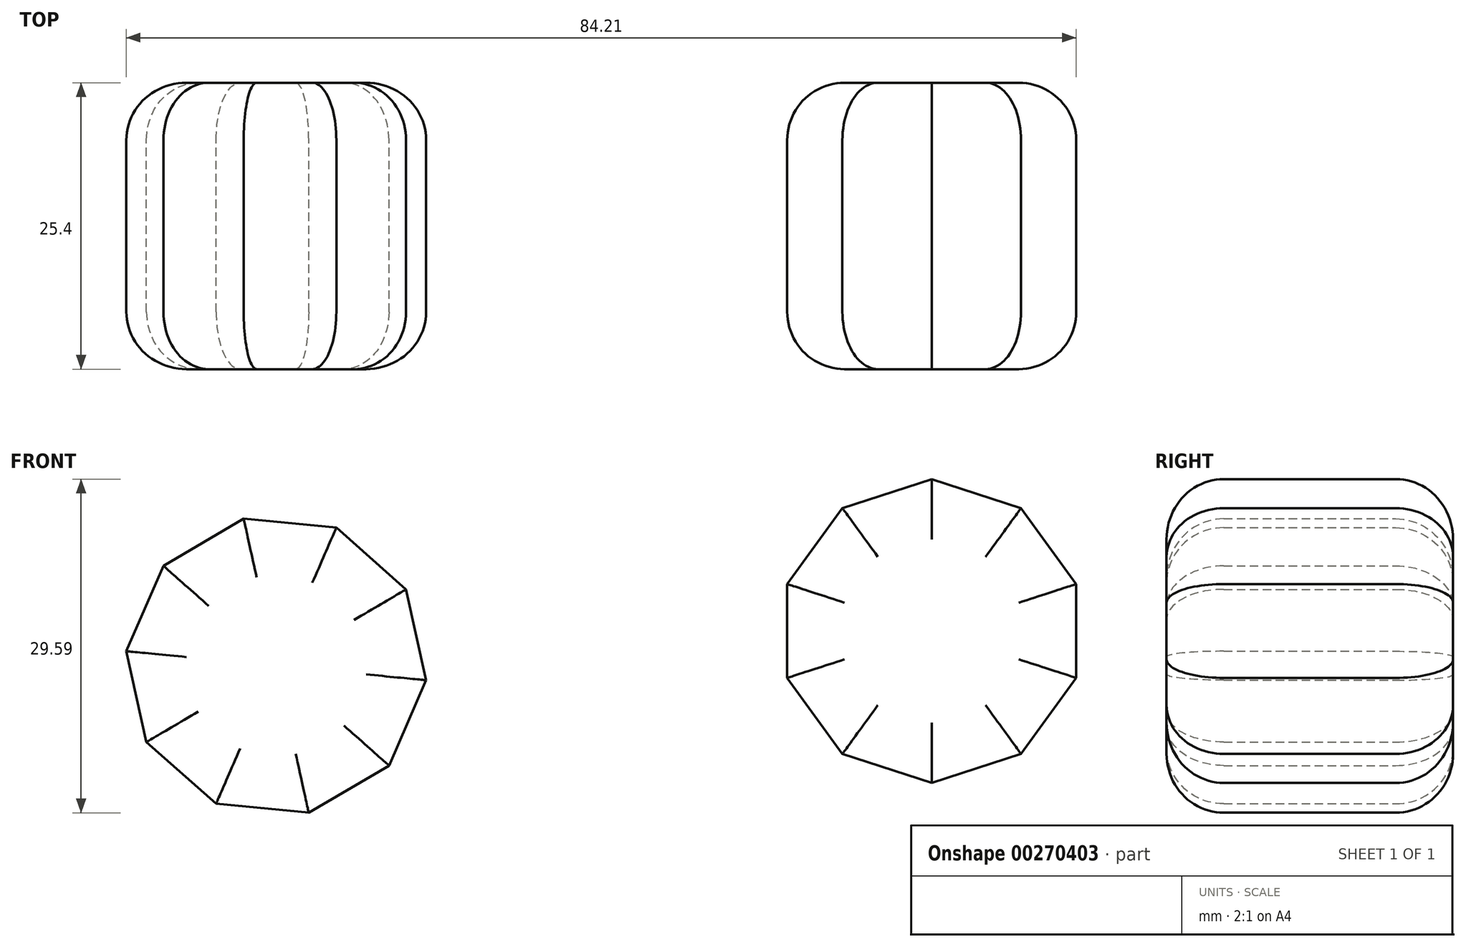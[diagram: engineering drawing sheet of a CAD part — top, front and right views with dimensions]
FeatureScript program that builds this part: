
annotation { "Feature Type Name" : "Feature", "Feature Type Description" : "" }
export const myFeature = defineFeature(function(context is Context, id is Id, definition is map)
    precondition{}
    {
        {
            var Q0;
            Q0=qCreatedBy(makeId("Front.planeOp"),FACE);
            var sketch = newSketch(context, id + "F0", { "sketchPlane" : qUnion([Q0])});
            skCircle(sketch, "E0.cCircle", {"center": v(0, 2.58) * mm, "radius": 12.7 * mm, "construction": true});
            skLineSegment(sketch, "E0.0", {"start": v(11.5, 9.35) * mm, "end": v(13.3, 1.3) * mm});
            skLineSegment(sketch, "E0.1", {"start": v(13.3, 1.3) * mm, "end": v(10, -6.27) * mm});
            skLineSegment(sketch, "E0.2", {"start": v(10, -6.27) * mm, "end": v(2.88, -10.46) * mm});
            skLineSegment(sketch, "E0.3", {"start": v(2.88, -10.46) * mm, "end": v(-5.33, -9.66) * mm});
            skLineSegment(sketch, "E0.4", {"start": v(-5.33, -9.66) * mm, "end": v(-11.5, -4.2) * mm});
            skLineSegment(sketch, "E0.5", {"start": v(-11.5, -4.2) * mm, "end": v(-13.3, 3.87) * mm});
            skLineSegment(sketch, "E0.6", {"start": v(-13.3, 3.87) * mm, "end": v(-10, 11.44) * mm});
            skLineSegment(sketch, "E0.7", {"start": v(-10, 11.44) * mm, "end": v(-2.88, 15.62) * mm});
            skLineSegment(sketch, "E0.8", {"start": v(-2.88, 15.62) * mm, "end": v(5.33, 14.83) * mm});
            skLineSegment(sketch, "E0.9", {"start": v(5.33, 14.83) * mm, "end": v(11.5, 9.35) * mm});
            skPoint(sketch, "E0.0.midPoint", {"position": v(12.4, 5.33) * mm});
            skCircle(sketch, "E1.cCircle", {"center": v(58.1, 5.66) * mm, "radius": 12.81 * mm, "construction": true});
            skLineSegment(sketch, "E1.0", {"start": v(70.92, 9.82) * mm, "end": v(70.92, 1.5) * mm});
            skLineSegment(sketch, "E1.1", {"start": v(70.92, 1.5) * mm, "end": v(66.02, -5.24) * mm});
            skLineSegment(sketch, "E1.2", {"start": v(66.02, -5.24) * mm, "end": v(58.1, -7.81) * mm});
            skLineSegment(sketch, "E1.3", {"start": v(58.1, -7.81) * mm, "end": v(50.19, -5.24) * mm});
            skLineSegment(sketch, "E1.4", {"start": v(50.19, -5.24) * mm, "end": v(45.3, 1.5) * mm});
            skLineSegment(sketch, "E1.5", {"start": v(45.3, 1.5) * mm, "end": v(45.3, 9.82) * mm});
            skLineSegment(sketch, "E1.6", {"start": v(45.3, 9.82) * mm, "end": v(50.19, 16.56) * mm});
            skLineSegment(sketch, "E1.7", {"start": v(50.19, 16.56) * mm, "end": v(58.1, 19.13) * mm});
            skLineSegment(sketch, "E1.8", {"start": v(58.1, 19.13) * mm, "end": v(66.02, 16.56) * mm});
            skLineSegment(sketch, "E1.9", {"start": v(66.02, 16.56) * mm, "end": v(70.92, 9.82) * mm});
            skPoint(sketch, "E1.0.midPoint", {"position": v(70.92, 5.66) * mm});
            skSolve(sketch);
        }
        {
            var Q0;
            Q0 = qSketchRegion(id + "F0", true);
            extrude(context, id + "F1", {"entities" : qUnion([Q0]), "depth" : 25.4 * mm});
        }
        {
            var Q0;
            Q0=makeQuery(id+"F1.opExtrude","CAP_FACE",FACE,{"disambiguationData":[OSD([sQuery(id+"F0.wireOp",EDGE,"E0.0"),sQuery(id+"F0.wireOp",EDGE,"E0.1"),sQuery(id+"F0.wireOp",EDGE,"E0.2"),sQuery(id+"F0.wireOp",EDGE,"E0.3"),sQuery(id+"F0.wireOp",EDGE,"E0.4"),sQuery(id+"F0.wireOp",EDGE,"E0.5"),sQuery(id+"F0.wireOp",EDGE,"E0.6"),sQuery(id+"F0.wireOp",EDGE,"E0.7"),sQuery(id+"F0.wireOp",EDGE,"E0.8"),sQuery(id+"F0.wireOp",EDGE,"E0.9")])],"isStart":false});
            var Q1;
            Q1=makeQuery(id+"F1.opExtrude","CAP_FACE",FACE,{"disambiguationData":[OSD([sQuery(id+"F0.wireOp",EDGE,"E1.0"),sQuery(id+"F0.wireOp",EDGE,"E1.1"),sQuery(id+"F0.wireOp",EDGE,"E1.2"),sQuery(id+"F0.wireOp",EDGE,"E1.3"),sQuery(id+"F0.wireOp",EDGE,"E1.4"),sQuery(id+"F0.wireOp",EDGE,"E1.5"),sQuery(id+"F0.wireOp",EDGE,"E1.6"),sQuery(id+"F0.wireOp",EDGE,"E1.7"),sQuery(id+"F0.wireOp",EDGE,"E1.8"),sQuery(id+"F0.wireOp",EDGE,"E1.9")])],"isStart":false});
            var Q2;
            Q2=makeQuery(id+"F1.opExtrude","CAP_FACE",FACE,{"disambiguationData":[OSD([sQuery(id+"F0.wireOp",EDGE,"E0.0"),sQuery(id+"F0.wireOp",EDGE,"E0.1"),sQuery(id+"F0.wireOp",EDGE,"E0.2"),sQuery(id+"F0.wireOp",EDGE,"E0.3"),sQuery(id+"F0.wireOp",EDGE,"E0.4"),sQuery(id+"F0.wireOp",EDGE,"E0.5"),sQuery(id+"F0.wireOp",EDGE,"E0.6"),sQuery(id+"F0.wireOp",EDGE,"E0.7"),sQuery(id+"F0.wireOp",EDGE,"E0.8"),sQuery(id+"F0.wireOp",EDGE,"E0.9")])],"isStart":true});
            var Q3;
            Q3=makeQuery(id+"F1.opExtrude","CAP_FACE",FACE,{"disambiguationData":[OSD([sQuery(id+"F0.wireOp",EDGE,"E1.0"),sQuery(id+"F0.wireOp",EDGE,"E1.1"),sQuery(id+"F0.wireOp",EDGE,"E1.2"),sQuery(id+"F0.wireOp",EDGE,"E1.3"),sQuery(id+"F0.wireOp",EDGE,"E1.4"),sQuery(id+"F0.wireOp",EDGE,"E1.5"),sQuery(id+"F0.wireOp",EDGE,"E1.6"),sQuery(id+"F0.wireOp",EDGE,"E1.7"),sQuery(id+"F0.wireOp",EDGE,"E1.8"),sQuery(id+"F0.wireOp",EDGE,"E1.9")])],"isStart":true});
            fillet(context, id + "F2", {"entities" : qUnion([Q0, Q1, Q2, Q3]), "radius" : 5.08 * mm, "tangentPropagation" : true, "allowEdgeOverflow" : false});
        }
    });
